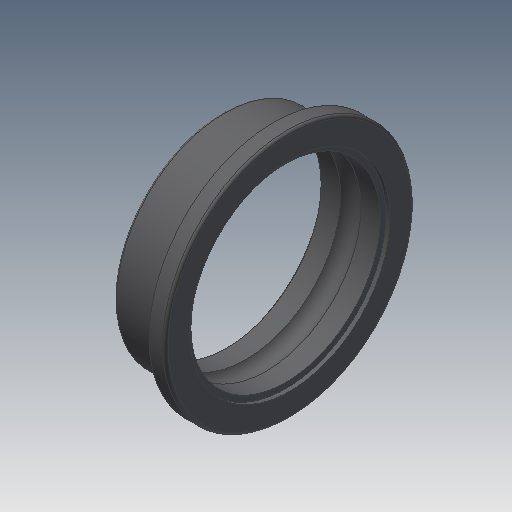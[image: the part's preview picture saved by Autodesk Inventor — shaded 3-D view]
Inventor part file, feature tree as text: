
AUTODESK INVENTOR PART (.ipt)
format: ipt  version: 2019.4 (Build 234330000, 330)  size: 186,368 bytes
history: native  units: mm
features: other x14, revolve x1, sketch x1
ambient origin geometry x8: Origin, YZ Plane, XZ Plane, XY Plane, X Axis, Y Axis, Z Axis, Center Point
bodies: Solid1 (feature_tree)
feature tree (16):
  revolve  "Revolution1"  [1 undecoded]
  other  "ip_st_1_XY"
  other  "ip_st_1_YZ"
  other  "ip_st_1_ZX"
  other  "ip_st_1_X"
  other  "ip_st_1_Y"
  other  "ip_st_1_Z"
  other  "ip_st_1_Center"
  other  "ip_st_2_XY"
  other  "ip_st_2_YZ"
  other  "ip_st_2_ZX"
  other  "ip_st_2_X"
  other  "ip_st_2_Y"
  other  "ip_st_2_Z"
  other  "ip_st_2_Center"
  sketch  "Sketch_1"  dims[d0=360.0deg d1=0.0mm d2=0.0mm]
note: 1 required parameter value undecoded (feature->parameter linkage not recoverable at this tier; creation-order binding heuristic only, values carry confidence <= 0.55)
